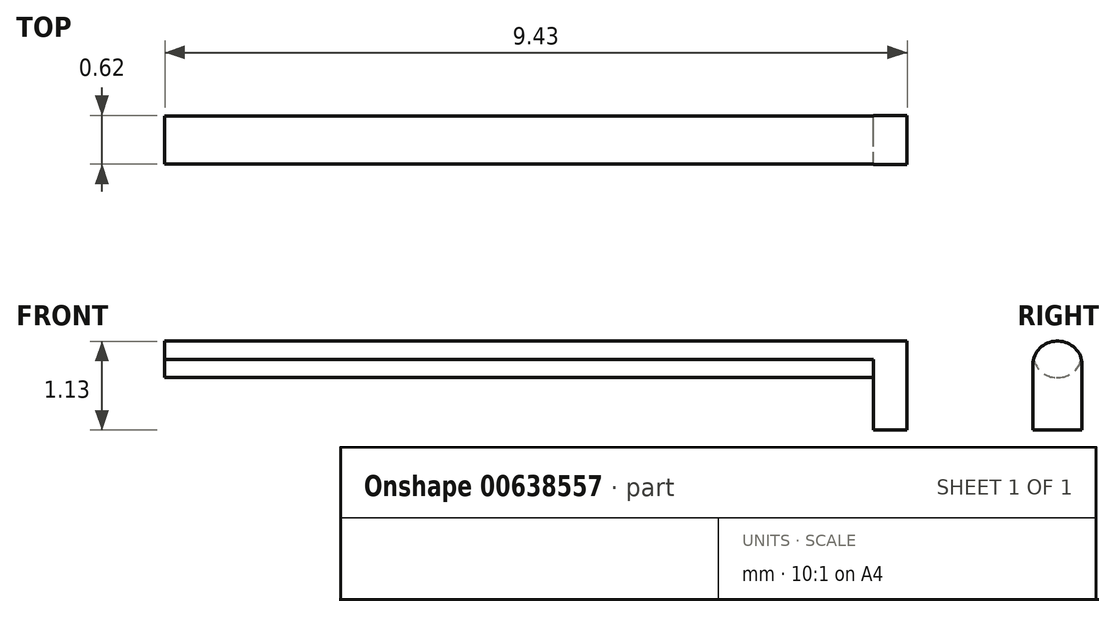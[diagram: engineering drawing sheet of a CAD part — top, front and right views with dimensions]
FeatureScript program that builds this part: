
annotation { "Feature Type Name" : "Feature", "Feature Type Description" : "" }
export const myFeature = defineFeature(function(context is Context, id is Id, definition is map)
    precondition{}
    {
        {
            var Q0;
            Q0=qCreatedBy(makeId("Front.planeOp"),FACE);
            var sketch = newSketch(context, id + "F0", { "sketchPlane" : qUnion([Q0])});
            skLineSegment(sketch, "E0.bottom", {"start": v(-58.01, 12.4) * mm, "end": v(17.4, 12.4) * mm});
            skLineSegment(sketch, "E0.top", {"start": v(-58.01, 8.7) * mm, "end": v(17.4, 8.7) * mm});
            skLineSegment(sketch, "E0.left", {"start": v(-58.01, 12.4) * mm, "end": v(-58.01, 8.7) * mm});
            skLineSegment(sketch, "E0.right", {"start": v(17.4, 12.4) * mm, "end": v(17.4, 8.7) * mm});
            skLineSegment(sketch, "E1.bottom", {"start": v(17.4, 8.7) * mm, "end": v(14.02, 8.7) * mm});
            skLineSegment(sketch, "E1.top", {"start": v(17.4, 3.4) * mm, "end": v(14.02, 3.4) * mm});
            skLineSegment(sketch, "E1.left", {"start": v(17.4, 8.7) * mm, "end": v(17.4, 3.4) * mm});
            skLineSegment(sketch, "E1.right", {"start": v(14.02, 8.7) * mm, "end": v(14.02, 3.4) * mm});
            skSolve(sketch);
        }
        {
            var Q0;
            Q0 = qSketchRegion(id + "F0", true);
            extrude(context, id + "F1", {"entities" : qUnion([Q0]), "depth" : 5 * mm, "offsetDistance" : 25 * mm});
        }
        {
            var Q0;
            Q0=makeQuery(id+"F1.opExtrude","CAP_EDGE",EDGE,{"disambiguationData":[OSD([sQuery(id+"F0.wireOp",EDGE,"E0.bottom")])],"isStart":true});
            var Q1;
            Q1=makeQuery(id+"F1.opExtrude","CAP_EDGE",EDGE,{"disambiguationData":[OSD([sQuery(id+"F0.wireOp",EDGE,"E0.bottom")])],"isStart":false});
            var Q2;
            Q2=makeQuery(id+"F1.opExtrude","CAP_EDGE",EDGE,{"disambiguationData":[OSD([sQuery(id+"F0.wireOp",EDGE,"E0.top")])],"isStart":true});
            var Q3;
            Q3=makeQuery(id+"F1.opExtrude","CAP_EDGE",EDGE,{"disambiguationData":[OSD([sQuery(id+"F0.wireOp",EDGE,"E0.top")])],"isStart":false});
            fillet(context, id + "F2", {"entities" : qUnion([Q0, Q1, Q2, Q3]), "radius" : 2.41 * mm, "tangentPropagation" : true, "allowEdgeOverflow" : false});
        }
        {
            var Q0;
            Q0=makeQuery(id+"F1.opExtrude","SWEPT_BODY",BODY,{"disambiguationData":[OSD([sQuery(id+"F0.wireOp",EDGE,"E0.bottom"),sQuery(id+"F0.wireOp",EDGE,"E0.top"),sQuery(id+"F0.wireOp",EDGE,"E0.left"),sQuery(id+"F0.wireOp",EDGE,"E0.right"),sQuery(id+"F0.wireOp",EDGE,"E1.top"),sQuery(id+"F0.wireOp",EDGE,"E1.left"),sQuery(id+"F0.wireOp",EDGE,"E1.right")])]});
            var Q1;
            Q1=qCreatedBy(makeId("Origin.pointOp"),VERTEX);
            transform(context, id + "F3", {"entities" : qUnion([Q0]), "transformType" : TransformType.SCALE_UNIFORMLY, "scale" : 0.12, "scalePoint" : qUnion([Q1]), "makeCopy" : false});
        }
    });
